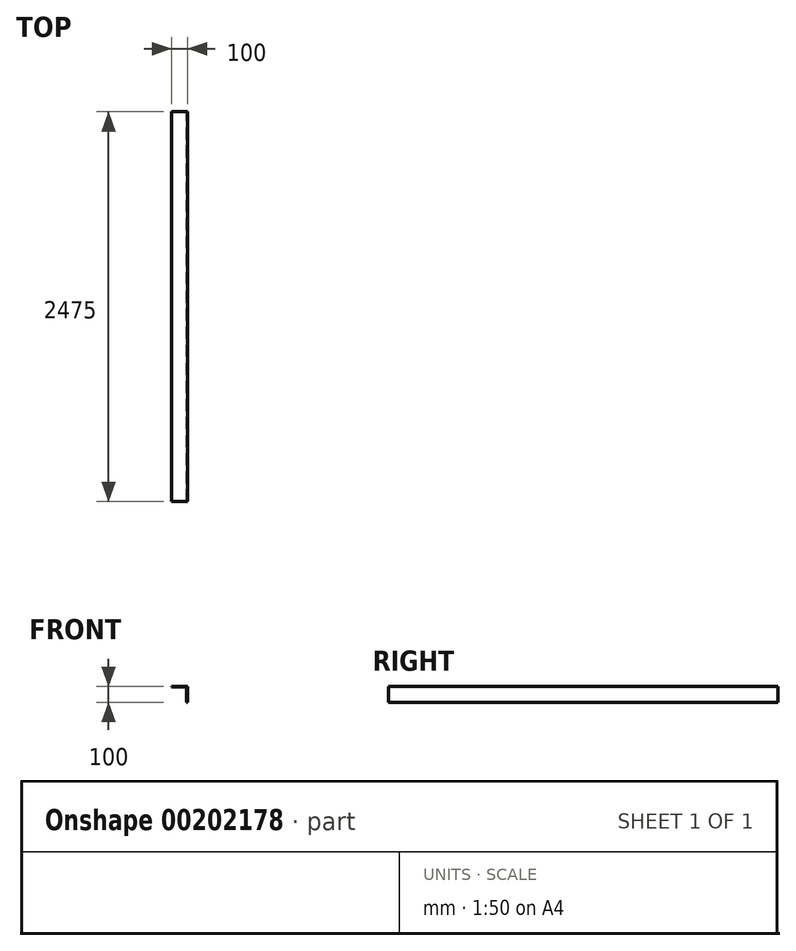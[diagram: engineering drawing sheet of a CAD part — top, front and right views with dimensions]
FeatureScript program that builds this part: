
annotation { "Feature Type Name" : "Feature", "Feature Type Description" : "" }
export const myFeature = defineFeature(function(context is Context, id is Id, definition is map)
    precondition{}
    {
        {
            var Q0;
            Q0=qCreatedBy(makeId("Front.planeOp"),FACE);
            var sketch = newSketch(context, id + "F0", { "sketchPlane" : qUnion([Q0])});
            skLineSegment(sketch, "E0", {"start": v(0, 0) * mm, "end": v(100, 0) * mm});
            skLineSegment(sketch, "E1", {"start": v(100, 0) * mm, "end": v(100, -100) * mm});
            skLineSegment(sketch, "E2", {"start": v(100, -100) * mm, "end": v(96, -100) * mm});
            skLineSegment(sketch, "E3", {"start": v(96, -100) * mm, "end": v(96, -4) * mm});
            skLineSegment(sketch, "E4", {"start": v(96, -4) * mm, "end": v(0, -4) * mm});
            skLineSegment(sketch, "E5", {"start": v(0, -4) * mm, "end": v(0, 0) * mm});
            skSolve(sketch);
        }
        {
            var Q0;
            Q0=qSketchRegion(id+"F0",true);
            extrude(context, id + "F1", {"entities" : qUnion([Q0]), "depth" : 2475 * mm});
        }
    });
